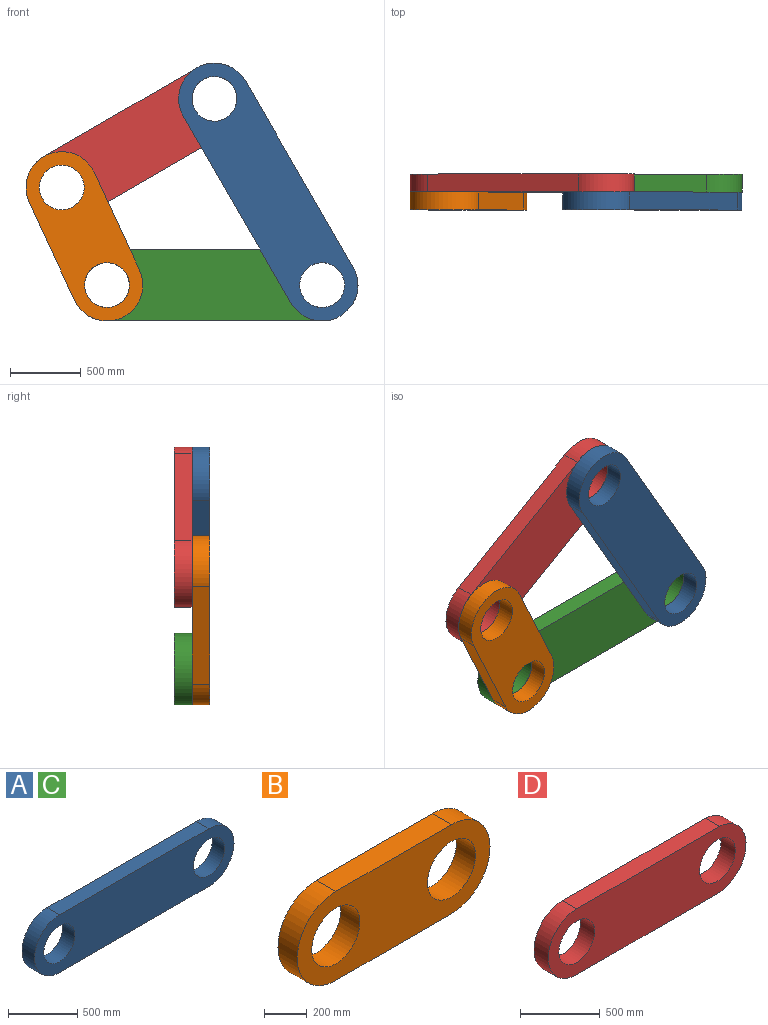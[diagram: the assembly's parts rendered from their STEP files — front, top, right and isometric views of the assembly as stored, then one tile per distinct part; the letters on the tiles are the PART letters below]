
ASSEMBLY  parts=4 mates=7
PART A: 8 faces, bbox 2032x127x508 mm
  f0: cylinder r=254mm len=508mm, axis (0,1,0), area 101341.5mm2, adj f1,f5,f6,f7
  f1: plane 1524x127mm, normal (0,0,-1), area 193548mm2, adj f0,f2,f6,f7
  f2: cylinder r=254mm len=508mm, axis (0,1,0), area 101341.5mm2, adj f1,f5,f6,f7
  f3: cylinder r=158.75mm len=317.5mm, axis (0,1,0), area 126676.9mm2, adj f6,f7
  f4: cylinder r=158.75mm len=317.5mm, axis (0,1,0), area 126676.9mm2, adj f6,f7
  f5: plane 1524x127mm, normal (0,0,1), area 193548mm2, adj f0,f2,f6,f7
  f6: plane 2032x508mm, normal (0,-1,0), area 818528.9mm2, adj f0,f1,f2,f3,f4,f5
  f7: plane 2032x508mm, normal (0,1,0), area 818528.9mm2, adj f0,f1,f2,f3,f4,f5
PART B: 8 faces, bbox 1270x127x508 mm
  f0: cylinder r=254mm len=508mm, axis (0,1,0), area 101341.5mm2, adj f1,f5,f6,f7
  f1: plane 762x127mm, normal (0,0,-1), area 96774mm2, adj f0,f2,f6,f7
  f2: cylinder r=254mm len=508mm, axis (0,1,0), area 101341.5mm2, adj f1,f5,f6,f7
  f3: cylinder r=158.75mm len=317.5mm, axis (0,1,0), area 126676.9mm2, adj f6,f7
  f4: cylinder r=158.75mm len=317.5mm, axis (0,1,0), area 126676.9mm2, adj f6,f7
  f5: plane 762x127mm, normal (0,0,1), area 96774mm2, adj f0,f2,f6,f7
  f6: plane 1270x508mm, normal (0,-1,0), area 431432.9mm2, adj f0,f1,f2,f3,f4,f5
  f7: plane 1270x508mm, normal (0,1,0), area 431432.9mm2, adj f0,f1,f2,f3,f4,f5
PART C: same geometry as A
PART D: 8 faces, bbox 1757.5x127x507.2 mm
  f0: cylinder r=253.23mm len=506.46mm, axis (0,1,0), area 101035mm2, adj f1,f5,f6,f7
  f1: plane 1230.52x127mm, normal (0,0,-1), area 156276.2mm2, adj f0,f2,f6,f7
  f2: cylinder r=254mm len=507.23mm, axis (0,1,0), area 101341.5mm2, adj f1,f5,f6,f7
  f3: cylinder r=158.75mm len=317.5mm, axis (0,1,0), area 126676.9mm2, adj f6,f7
  f4: cylinder r=158.75mm len=317.5mm, axis (0,1,0), area 126676.9mm2, adj f6,f7
  f5: plane 1270x127mm, normal (0,0,1), area 161290mm2, adj f0,f2,f6,f7
  f6: plane 1757.49x507.23mm, normal (0,-1,0), area 676936.3mm2, adj f0,f1,f2,f3,f4,f5
  f7: plane 1757.49x507.23mm, normal (0,1,0), area 676936.3mm2, adj f0,f1,f2,f3,f4,f5
PLACE A rot(axis=(0,1,0),60deg) t=(474.02,-63.5,630.86)mm
PLACE B rot(axis=(0,1,0),65.2deg) t=(-828.59,-63.5,316.96)mm
PLACE C t=(93.49,63.5,-28.78)mm fixed
PLACE D rot(axis=(-0.97,0,-0.26),180deg) t=(-456.6,-63.5,971.64)mm
MATE cylindrical A.f2 <-> C.f2  axis (0,-1,0) through (855.49,-190.5,-28.78)mm
MATE planar C.f6 <-> A.f7  axis (0,-1,0) through (93.49,-63.5,-28.78)mm
MATE cylindrical C.f0 <-> B.f2  axis (0,-1,0) through (-668.51,-63.5,-28.78)mm
MATE cylindrical B.f0 <-> D.f3  axis (0,1,0) through (-988.67,-63.5,662.7)mm
MATE cylindrical D.f2 <-> A.f0  axis (0,-1,0) through (92.55,-63.5,1290.5)mm
MATE planar C.f6 <-> B.f7  axis (0,-1,0) through (93.49,-63.5,-28.78)mm
MATE planar C.f7 <-> D.f6  axis (0,1,0) through (93.49,63.5,-28.78)mm
